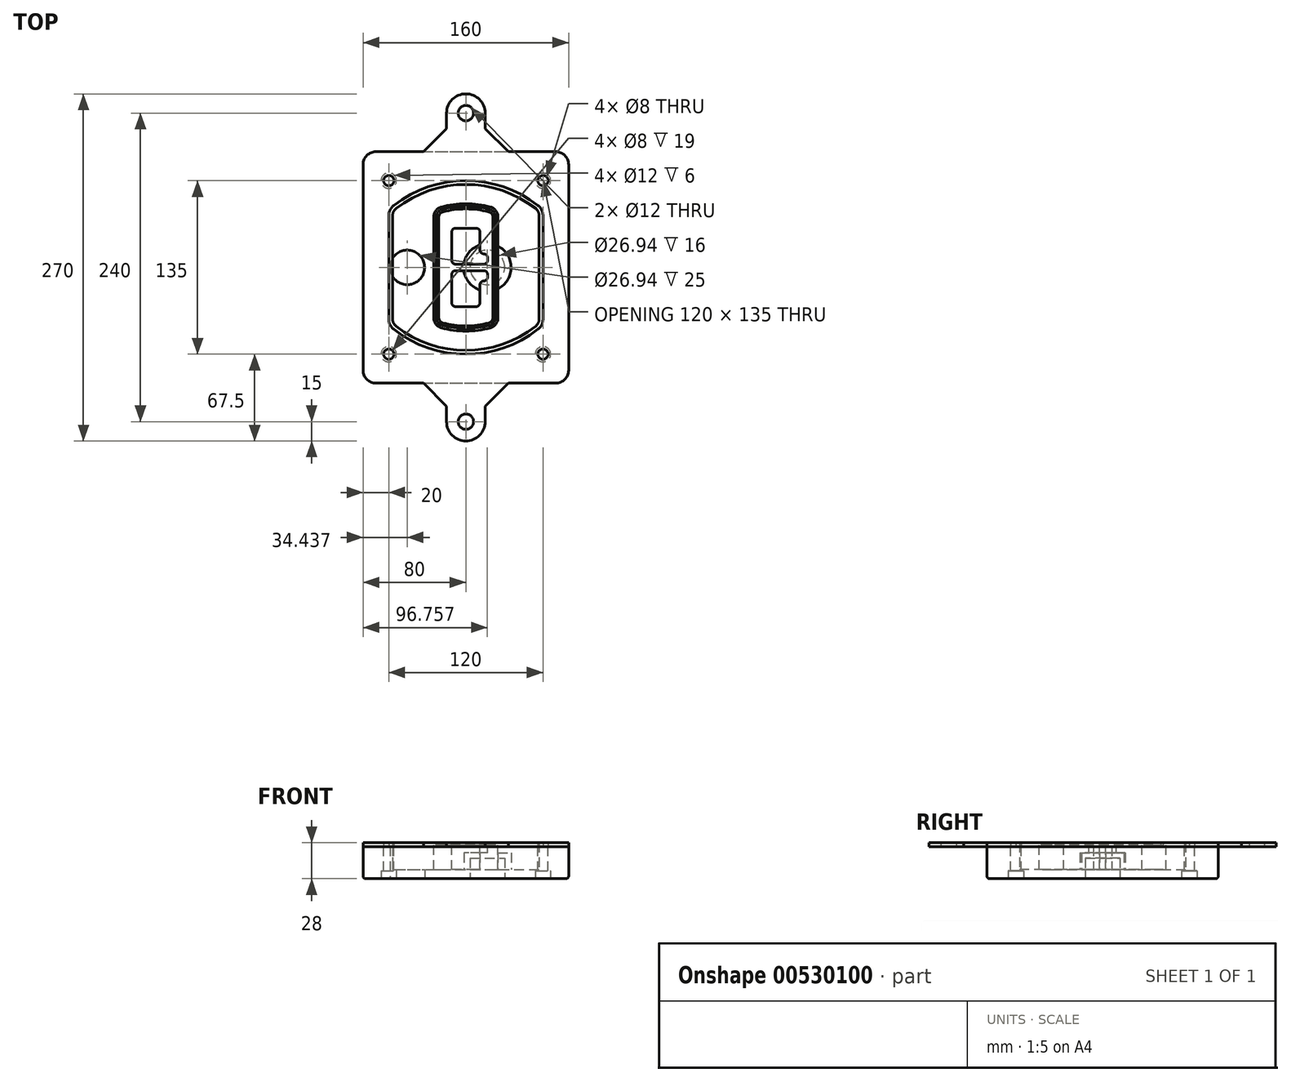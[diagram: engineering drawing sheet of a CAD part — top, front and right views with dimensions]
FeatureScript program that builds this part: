
annotation { "Feature Type Name" : "Feature", "Feature Type Description" : "" }
export const myFeature = defineFeature(function(context is Context, id is Id, definition is map)
    precondition{}
    {
        {
            var Q0;
            Q0=qCreatedBy(makeId("Top.planeOp"),FACE);
            var sketch = newSketch(context, id + "F0", { "sketchPlane" : qUnion([Q0])});
            skPoint(sketch, "E0.rect.middle", {"position": v(0, 0) * mm});
            skLineSegment(sketch, "E1.bottom", {"start": v(-70, -90) * mm, "end": v(70, -90) * mm});
            skLineSegment(sketch, "E1.top", {"start": v(-70, 90) * mm, "end": v(70, 90) * mm});
            skLineSegment(sketch, "E1.left", {"start": v(-80, -80) * mm, "end": v(-80, 80) * mm});
            skLineSegment(sketch, "E1.right", {"start": v(80, -80) * mm, "end": v(80, 80) * mm});
            skLineSegment(sketch, "E2", {"start": v(-80, 90) * mm, "end": v(80, -90) * mm, "construction": true});
            skLineSegment(sketch, "E3", {"start": v(80, 90) * mm, "end": v(-80, -90) * mm, "construction": true});
            skCircle(sketch, "E4", {"center": v(-60, 67.5) * mm, "radius": 4 * mm});
            skCircle(sketch, "E5", {"center": v(60, 67.5) * mm, "radius": 4 * mm});
            skCircle(sketch, "E6", {"center": v(60, -67.5) * mm, "radius": 4 * mm});
            skCircle(sketch, "E7", {"center": v(-60, -67.5) * mm, "radius": 4 * mm});
            skLineSegment(sketch, "E8", {"start": v(-60, 67.5) * mm, "end": v(60, 67.5) * mm, "construction": true});
            skLineSegment(sketch, "E9", {"start": v(60, 67.5) * mm, "end": v(60, -67.5) * mm, "construction": true});
            skLineSegment(sketch, "E10", {"start": v(60, -67.5) * mm, "end": v(-60, -67.5) * mm, "construction": true});
            skLineSegment(sketch, "E11", {"start": v(-60, -67.5) * mm, "end": v(-60, 67.5) * mm, "construction": true});
            skLineSegment(sketch, "E12", {"start": v(-60, 40.3) * mm, "end": v(-60, -40.3) * mm});
            skLineSegment(sketch, "E13", {"start": v(60, 40.3) * mm, "end": v(60, -40.3) * mm});
            skArc(sketch, "E14", {"start": v(56.15, 48.18) * mm, "mid": v(0, 67.5) * mm, "end": v(-56.15, 48.18) * mm});
            skArc(sketch, "E15", {"start": v(-56.15, -48.18) * mm, "mid": v(0, -67.5) * mm, "end": v(56.15, -48.18) * mm});
            skLineSegment(sketch, "E16", {"start": v(-60, 0) * mm, "end": v(60, 0) * mm, "construction": true});
            skPoint(sketch, "E17.visualSharp", {"position": v(-60, -45) * mm});
            skArc(sketch, "E17.filletArc", {"start": v(-60, -40.3) * mm, "mid": v(-58.99, -44.68) * mm, "end": v(-56.15, -48.18) * mm});
            skPoint(sketch, "E18.visualSharp", {"position": v(-60, 45) * mm});
            skArc(sketch, "E18.filletArc", {"start": v(-56.15, 48.18) * mm, "mid": v(-58.99, 44.68) * mm, "end": v(-60, 40.3) * mm});
            skPoint(sketch, "E19.visualSharp", {"position": v(60, 45) * mm});
            skArc(sketch, "E19.filletArc", {"start": v(60, 40.3) * mm, "mid": v(58.99, 44.68) * mm, "end": v(56.15, 48.18) * mm});
            skPoint(sketch, "E20.visualSharp", {"position": v(60, -45) * mm});
            skArc(sketch, "E20.filletArc", {"start": v(56.15, -48.18) * mm, "mid": v(58.99, -44.68) * mm, "end": v(60, -40.3) * mm});
            skPoint(sketch, "E21.visualSharp", {"position": v(-80, 90) * mm});
            skArc(sketch, "E21.filletArc", {"start": v(-70, 90) * mm, "mid": v(-77.07, 87.07) * mm, "end": v(-80, 80) * mm});
            skPoint(sketch, "E22.visualSharp", {"position": v(80, 90) * mm});
            skArc(sketch, "E22.filletArc", {"start": v(80, 80) * mm, "mid": v(77.07, 87.07) * mm, "end": v(70, 90) * mm});
            skPoint(sketch, "E23.visualSharp", {"position": v(80, -90) * mm});
            skArc(sketch, "E23.filletArc", {"start": v(70, -90) * mm, "mid": v(77.07, -87.07) * mm, "end": v(80, -80) * mm});
            skPoint(sketch, "E24.visualSharp", {"position": v(-80, -90) * mm});
            skArc(sketch, "E24.filletArc", {"start": v(-80, -80) * mm, "mid": v(-77.07, -87.07) * mm, "end": v(-70, -90) * mm});
            skArc(sketch, "E25.0", {"start": v(57, 40.3) * mm, "mid": v(56.3, 43.36) * mm, "end": v(54.3, 45.81) * mm});
            skLineSegment(sketch, "E25.1", {"start": v(57, 40.3) * mm, "end": v(57, -40.3) * mm});
            skArc(sketch, "E25.2", {"start": v(54.3, -45.81) * mm, "mid": v(56.3, -43.36) * mm, "end": v(57, -40.3) * mm});
            skArc(sketch, "E25.3", {"start": v(-54.3, -45.81) * mm, "mid": v(0, -64.5) * mm, "end": v(54.3, -45.81) * mm});
            skArc(sketch, "E25.4", {"start": v(-57, -40.3) * mm, "mid": v(-56.3, -43.36) * mm, "end": v(-54.3, -45.81) * mm});
            skArc(sketch, "E25.5", {"start": v(54.3, 45.81) * mm, "mid": v(0, 64.5) * mm, "end": v(-54.3, 45.81) * mm});
            skLineSegment(sketch, "E25.6", {"start": v(-57, 40.3) * mm, "end": v(-57, -40.3) * mm});
            skArc(sketch, "E25.7", {"start": v(-54.3, 45.81) * mm, "mid": v(-56.3, 43.36) * mm, "end": v(-57, 40.3) * mm});
            skArc(sketch, "E26.0", {"start": v(-58.62, 51.33) * mm, "mid": v(-62.58, 46.43) * mm, "end": v(-64, 40.3) * mm});
            skArc(sketch, "E26.1", {"start": v(58.62, 51.33) * mm, "mid": v(0, 71.5) * mm, "end": v(-58.62, 51.33) * mm});
            skArc(sketch, "E26.2", {"start": v(64, 40.3) * mm, "mid": v(62.58, 46.43) * mm, "end": v(58.62, 51.33) * mm});
            skLineSegment(sketch, "E26.3", {"start": v(64, 40.3) * mm, "end": v(64, -40.3) * mm});
            skArc(sketch, "E26.4", {"start": v(58.62, -51.33) * mm, "mid": v(62.58, -46.43) * mm, "end": v(64, -40.3) * mm});
            skLineSegment(sketch, "E26.5", {"start": v(-64, 40.3) * mm, "end": v(-64, -40.3) * mm});
            skArc(sketch, "E26.6", {"start": v(-58.62, -51.33) * mm, "mid": v(0, -71.5) * mm, "end": v(58.62, -51.33) * mm});
            skArc(sketch, "E26.7", {"start": v(-64, -40.3) * mm, "mid": v(-62.58, -46.43) * mm, "end": v(-58.62, -51.33) * mm});
            skSolve(sketch);
        }
        {
            var Q0;
            Q0=makeQuery(id+"F0.imprint","IMPRINT",FACE,{"disambiguationData":[TD([[makeQuery(id+"F0.imprint","IMPRINT",EDGE,{"derivedFrom":sQuery(id+"F0.wireOp",EDGE,"E1.bottom")}),1.0]])]});
            var Q1;
            Q1=makeQuery(id+"F0.imprint","IMPRINT",FACE,{"disambiguationData":[TD([[makeQuery(id+"F0.imprint","IMPRINT",EDGE,{"derivedFrom":sQuery(id+"F0.wireOp",EDGE,"E12")}),1.0]])]});
            var Q2;
            Q2=makeQuery(id+"F0.imprint","IMPRINT",FACE,{"disambiguationData":[TD([[makeQuery(id+"F0.imprint","IMPRINT",EDGE,{"derivedFrom":sQuery(id+"F0.wireOp",EDGE,"E25.0")}),1.0]])]});
            var Q3;
            Q3=makeQuery(id+"F0.imprint","IMPRINT",FACE,{"disambiguationData":[TD([[makeQuery(id+"F0.imprint","IMPRINT",EDGE,{"derivedFrom":sQuery(id+"F0.wireOp",EDGE,"E12")}),-1.0]])]});
            extrude(context, id + "F1", {"entities" : qUnion([Q0, Q1, Q2, Q3]), "oppositeDirection" : true, "depth" : 25 * mm});
        }
        {
            var Q0;
            Q0=makeQuery(id+"F0.imprint","IMPRINT",FACE,{"disambiguationData":[TD([[makeQuery(id+"F0.imprint","IMPRINT",EDGE,{"derivedFrom":sQuery(id+"F0.wireOp",EDGE,"E12")}),1.0]])]});
            extrude(context, id + "F2", {"entities" : qUnion([Q0]), "operationType" : NewBodyOperationType.ADD, "depth" : 3 * mm, "offsetDistance" : 25 * mm});
        }
        {
            var Q0;
            Q0=makeQuery(id+"F0.imprint","IMPRINT",FACE,{"disambiguationData":[TD([[makeQuery(id+"F0.imprint","IMPRINT",EDGE,{"derivedFrom":sQuery(id+"F0.wireOp",EDGE,"E25.0")}),1.0]])]});
            extrude(context, id + "F3", {"entities" : qUnion([Q0]), "operationType" : NewBodyOperationType.REMOVE, "oppositeDirection" : true, "depth" : 18 * mm});
        }
        {
            var Q0;
            Q0=makeQuery(id+"F2.opExtrude","CAP_FACE",FACE,{"disambiguationData":[OSD([sQuery(id+"F0.wireOp",EDGE,"E12"),sQuery(id+"F0.wireOp",EDGE,"E13"),sQuery(id+"F0.wireOp",EDGE,"E14"),sQuery(id+"F0.wireOp",EDGE,"E15"),sQuery(id+"F0.wireOp",EDGE,"E17.filletArc"),sQuery(id+"F0.wireOp",EDGE,"E18.filletArc"),sQuery(id+"F0.wireOp",EDGE,"E19.filletArc"),sQuery(id+"F0.wireOp",EDGE,"E20.filletArc"),sQuery(id+"F0.wireOp",EDGE,"E25.0"),sQuery(id+"F0.wireOp",EDGE,"E25.1"),sQuery(id+"F0.wireOp",EDGE,"E25.2"),sQuery(id+"F0.wireOp",EDGE,"E25.3"),sQuery(id+"F0.wireOp",EDGE,"E25.4"),sQuery(id+"F0.wireOp",EDGE,"E25.5"),sQuery(id+"F0.wireOp",EDGE,"E25.6"),sQuery(id+"F0.wireOp",EDGE,"E25.7")])],"isStart":false});
            var sketch = newSketch(context, id + "F4", { "sketchPlane" : qUnion([Q0])});
            skArc(sketch, "E27.0", {"start": v(-19.08, -46.97) * mm, "mid": v(0, -49.5) * mm, "end": v(19.08, -46.97) * mm});
            skArc(sketch, "E28.0", {"start": v(19.08, 46.97) * mm, "mid": v(0, 49.5) * mm, "end": v(-19.08, 46.97) * mm});
            skLineSegment(sketch, "E29", {"start": v(-25, 39.25) * mm, "end": v(-25, -39.25) * mm});
            skLineSegment(sketch, "E30", {"start": v(25, 39.25) * mm, "end": v(25, -39.25) * mm});
            skLineSegment(sketch, "E31", {"start": v(-25, 45.1) * mm, "end": v(25, 45.1) * mm, "construction": true});
            skLineSegment(sketch, "E32", {"start": v(-25, -45.1) * mm, "end": v(25, -45.1) * mm, "construction": true});
            skPoint(sketch, "E33.visualSharp", {"position": v(-25, 45.1) * mm});
            skArc(sketch, "E33.filletArc", {"start": v(-19.08, 46.97) * mm, "mid": v(-23.35, 44.11) * mm, "end": v(-25, 39.25) * mm});
            skPoint(sketch, "E34.visualSharp", {"position": v(25, 45.1) * mm});
            skArc(sketch, "E34.filletArc", {"start": v(25, 39.25) * mm, "mid": v(23.35, 44.11) * mm, "end": v(19.08, 46.97) * mm});
            skPoint(sketch, "E35.visualSharp", {"position": v(25, -45.1) * mm});
            skArc(sketch, "E35.filletArc", {"start": v(19.08, -46.97) * mm, "mid": v(23.35, -44.11) * mm, "end": v(25, -39.25) * mm});
            skPoint(sketch, "E36.visualSharp", {"position": v(-25, -45.1) * mm});
            skArc(sketch, "E36.filletArc", {"start": v(-25, -39.25) * mm, "mid": v(-23.35, -44.11) * mm, "end": v(-19.08, -46.97) * mm});
            skArc(sketch, "E37.0", {"start": v(54.3, 45.81) * mm, "mid": v(0, 64.5) * mm, "end": v(-54.3, 45.81) * mm});
            skArc(sketch, "E37.1", {"start": v(-54.3, 45.81) * mm, "mid": v(-56.3, 43.36) * mm, "end": v(-57, 40.3) * mm});
            skLineSegment(sketch, "E37.2", {"start": v(-57, 40.3) * mm, "end": v(-57, -40.3) * mm});
            skArc(sketch, "E37.3", {"start": v(-57, -40.3) * mm, "mid": v(-56.3, -43.36) * mm, "end": v(-54.3, -45.81) * mm});
            skArc(sketch, "E37.4", {"start": v(-54.3, -45.81) * mm, "mid": v(0, -64.5) * mm, "end": v(54.3, -45.81) * mm});
            skArc(sketch, "E37.5", {"start": v(54.3, -45.81) * mm, "mid": v(56.3, -43.36) * mm, "end": v(57, -40.3) * mm});
            skLineSegment(sketch, "E37.6", {"start": v(57, 40.3) * mm, "end": v(57, -40.3) * mm});
            skArc(sketch, "E37.7", {"start": v(57, 40.3) * mm, "mid": v(56.3, 43.36) * mm, "end": v(54.3, 45.81) * mm});
            skLineSegment(sketch, "E38.0", {"start": v(23, 39.25) * mm, "end": v(23, -39.25) * mm});
            skArc(sketch, "E38.1", {"start": v(18.56, -45.04) * mm, "mid": v(21.76, -42.9) * mm, "end": v(23, -39.25) * mm});
            skArc(sketch, "E38.2", {"start": v(-18.56, -45.04) * mm, "mid": v(0, -47.5) * mm, "end": v(18.56, -45.04) * mm});
            skArc(sketch, "E38.3", {"start": v(-23, -39.25) * mm, "mid": v(-21.76, -42.9) * mm, "end": v(-18.56, -45.04) * mm});
            skLineSegment(sketch, "E38.4", {"start": v(-23, 39.25) * mm, "end": v(-23, -39.25) * mm});
            skArc(sketch, "E38.5", {"start": v(23, 39.25) * mm, "mid": v(21.76, 42.9) * mm, "end": v(18.56, 45.04) * mm});
            skArc(sketch, "E38.6", {"start": v(-18.56, 45.04) * mm, "mid": v(-21.76, 42.9) * mm, "end": v(-23, 39.25) * mm});
            skArc(sketch, "E38.7", {"start": v(18.56, 45.04) * mm, "mid": v(0, 47.5) * mm, "end": v(-18.56, 45.04) * mm});
            skArc(sketch, "E39.0", {"start": v(21, 39.25) * mm, "mid": v(20.18, 41.68) * mm, "end": v(18.04, 43.1) * mm});
            skLineSegment(sketch, "E39.1", {"start": v(21, 39.25) * mm, "end": v(21, -39.25) * mm});
            skArc(sketch, "E39.2", {"start": v(18.04, -43.1) * mm, "mid": v(20.18, -41.68) * mm, "end": v(21, -39.25) * mm});
            skArc(sketch, "E39.3", {"start": v(-18.04, -43.1) * mm, "mid": v(0, -45.5) * mm, "end": v(18.04, -43.1) * mm});
            skArc(sketch, "E39.4", {"start": v(-21, -39.25) * mm, "mid": v(-20.18, -41.68) * mm, "end": v(-18.04, -43.1) * mm});
            skArc(sketch, "E39.5", {"start": v(18.04, 43.1) * mm, "mid": v(0, 45.5) * mm, "end": v(-18.04, 43.1) * mm});
            skLineSegment(sketch, "E39.6", {"start": v(-21, 39.25) * mm, "end": v(-21, -39.25) * mm});
            skArc(sketch, "E39.7", {"start": v(-18.04, 43.1) * mm, "mid": v(-20.18, 41.68) * mm, "end": v(-21, 39.25) * mm});
            skLineSegment(sketch, "E40", {"start": v(-25, 0) * mm, "end": v(25, 0) * mm, "construction": true});
            skLineSegment(sketch, "E41", {"start": v(-11, 5.5) * mm, "end": v(-11, 27.5) * mm});
            skLineSegment(sketch, "E42", {"start": v(-8, 30.5) * mm, "end": v(8, 30.5) * mm});
            skLineSegment(sketch, "E43", {"start": v(11, 27.5) * mm, "end": v(11, 13.5) * mm});
            skLineSegment(sketch, "E44", {"start": v(14, 10.5) * mm, "end": v(14, 10.5) * mm});
            skLineSegment(sketch, "E45", {"start": v(17, 7.5) * mm, "end": v(17, 5.5) * mm});
            skLineSegment(sketch, "E46", {"start": v(14, 2.5) * mm, "end": v(-8, 2.5) * mm});
            skPoint(sketch, "E47.visualSharp", {"position": v(-11, 30.5) * mm});
            skArc(sketch, "E47.filletArc", {"start": v(-8, 30.5) * mm, "mid": v(-10.12, 29.62) * mm, "end": v(-11, 27.5) * mm});
            skPoint(sketch, "E48.visualSharp", {"position": v(11, 30.5) * mm});
            skArc(sketch, "E48.filletArc", {"start": v(11, 27.5) * mm, "mid": v(10.12, 29.62) * mm, "end": v(8, 30.5) * mm});
            skPoint(sketch, "E49.visualSharp", {"position": v(11, 10.5) * mm});
            skArc(sketch, "E49.filletArc", {"start": v(11, 13.5) * mm, "mid": v(11.88, 11.38) * mm, "end": v(14, 10.5) * mm});
            skPoint(sketch, "E50.visualSharp", {"position": v(17, 10.5) * mm});
            skArc(sketch, "E50.filletArc", {"start": v(17, 7.5) * mm, "mid": v(16.12, 9.62) * mm, "end": v(14, 10.5) * mm});
            skPoint(sketch, "E51.visualSharp", {"position": v(17, 2.5) * mm});
            skArc(sketch, "E51.filletArc", {"start": v(14, 2.5) * mm, "mid": v(16.12, 3.38) * mm, "end": v(17, 5.5) * mm});
            skPoint(sketch, "E52.visualSharp", {"position": v(-11, 2.5) * mm});
            skArc(sketch, "E52.filletArc", {"start": v(-11, 5.5) * mm, "mid": v(-10.12, 3.38) * mm, "end": v(-8, 2.5) * mm});
            skLineSegment(sketch, "E53.0.MirrorCS", {"start": v(14, -2.5) * mm, "end": v(-8, -2.5) * mm});
            skArc(sketch, "E54.0.MirrorCS", {"start": v(-11, -5.5) * mm, "mid": v(-10.12, -3.38) * mm, "end": v(-8, -2.5) * mm});
            skLineSegment(sketch, "E55.0.MirrorCS", {"start": v(-11, -5.5) * mm, "end": v(-11, -27.5) * mm});
            skArc(sketch, "E56.0.MirrorCS", {"start": v(-8, -30.5) * mm, "mid": v(-10.12, -29.62) * mm, "end": v(-11, -27.5) * mm});
            skLineSegment(sketch, "E57.0.MirrorCS", {"start": v(-8, -30.5) * mm, "end": v(8, -30.5) * mm});
            skArc(sketch, "E58.0.MirrorCS", {"start": v(11, -27.5) * mm, "mid": v(10.12, -29.62) * mm, "end": v(8, -30.5) * mm});
            skLineSegment(sketch, "E59.0.MirrorCS", {"start": v(11, -27.5) * mm, "end": v(11, -13.5) * mm});
            skArc(sketch, "E60.0.MirrorCS", {"start": v(11, -13.5) * mm, "mid": v(11.88, -11.38) * mm, "end": v(14, -10.5) * mm});
            skArc(sketch, "E61.0.MirrorCS", {"start": v(17, -7.5) * mm, "mid": v(16.12, -9.62) * mm, "end": v(14, -10.5) * mm});
            skLineSegment(sketch, "E62.0.MirrorCS", {"start": v(17, -7.5) * mm, "end": v(17, -5.5) * mm});
            skArc(sketch, "E63.0.MirrorCS", {"start": v(14, -2.5) * mm, "mid": v(16.12, -3.38) * mm, "end": v(17, -5.5) * mm});
            skSolve(sketch);
        }
        {
            var Q0;
            Q0=makeQuery(id+"F4.imprint","IMPRINT",FACE,{"disambiguationData":[TD([[makeQuery(id+"F4.imprint","IMPRINT",EDGE,{"derivedFrom":sQuery(id+"F4.wireOp",EDGE,"E27.0")}),1.0]])]});
            var Q1;
            Q1=makeQuery(id+"F4.imprint","IMPRINT",FACE,{"disambiguationData":[TD([[makeQuery(id+"F4.imprint","IMPRINT",EDGE,{"derivedFrom":sQuery(id+"F4.wireOp",EDGE,"E38.0")}),-1.0]])]});
            var Q2;
            Q2=makeQuery(id+"F4.imprint","IMPRINT",FACE,{"disambiguationData":[TD([[makeQuery(id+"F4.imprint","IMPRINT",EDGE,{"derivedFrom":sQuery(id+"F4.wireOp",EDGE,"E39.0")}),1.0]])]});
            extrude(context, id + "F5", {"entities" : qUnion([Q0, Q1, Q2]), "operationType" : NewBodyOperationType.ADD, "endBound" : BoundingType.UP_TO_NEXT, "oppositeDirection" : true, "depth" : 25 * mm});
        }
        {
            var Q0;
            Q0=makeQuery(id+"F4.imprint","IMPRINT",FACE,{"disambiguationData":[TD([[makeQuery(id+"F4.imprint","IMPRINT",EDGE,{"derivedFrom":sQuery(id+"F4.wireOp",EDGE,"E38.0")}),-1.0]])]});
            extrude(context, id + "F6", {"entities" : qUnion([Q0]), "operationType" : NewBodyOperationType.REMOVE, "oppositeDirection" : true, "depth" : 2 * mm});
        }
        {
            var Q0;
            Q0=makeQuery(id+"F1.opExtrude","CAP_FACE",FACE,{"disambiguationData":[OSD([sQuery(id+"F0.wireOp",EDGE,"E1.bottom"),sQuery(id+"F0.wireOp",EDGE,"E1.top"),sQuery(id+"F0.wireOp",EDGE,"E1.left"),sQuery(id+"F0.wireOp",EDGE,"E1.right"),sQuery(id+"F0.wireOp",EDGE,"E4"),sQuery(id+"F0.wireOp",EDGE,"E5"),sQuery(id+"F0.wireOp",EDGE,"E6"),sQuery(id+"F0.wireOp",EDGE,"E7"),sQuery(id+"F0.wireOp",EDGE,"E21.filletArc"),sQuery(id+"F0.wireOp",EDGE,"E22.filletArc"),sQuery(id+"F0.wireOp",EDGE,"E23.filletArc"),sQuery(id+"F0.wireOp",EDGE,"E24.filletArc")])],"isStart":false});
            var sketch = newSketch(context, id + "F7", { "sketchPlane" : qUnion([Q0])});
            skCircle(sketch, "E64", {"center": v(16.76, 0) * mm, "radius": 13.47 * mm});
            skCircle(sketch, "E65", {"center": v(-45.56, 0) * mm, "radius": 13.47 * mm});
            skLineSegment(sketch, "E66", {"start": v(80, 0) * mm, "end": v(-80, 0) * mm});
            skCircle(sketch, "E67", {"center": v(16.76, 0) * mm, "radius": 18.47 * mm});
            skCircle(sketch, "E68", {"center": v(60, -67.5) * mm, "radius": 6 * mm});
            skCircle(sketch, "E69", {"center": v(-60, -67.5) * mm, "radius": 6 * mm});
            skCircle(sketch, "E70", {"center": v(-60, 67.5) * mm, "radius": 6 * mm});
            skCircle(sketch, "E71", {"center": v(60, 67.5) * mm, "radius": 6 * mm});
            skSolve(sketch);
        }
        {
            var Q0;
            {var subQ1=sQuery(id+"F7.wireOp",EDGE,"E66");var subQ4=sQuery(id+"F7.wireOp",EDGE,"E64");var subQ6=makeQuery(id+"F7.imprint","INTERSECT",VERTEX,{"disambiguationData":[OD(0.0)],"derivedFrom":[subQ4,subQ1]});Q0=makeQuery(id+"F7.imprint","IMPRINT",FACE,{"disambiguationData":[TD([[makeQuery(id+"F7.imprint","IMPRINT",EDGE,{"disambiguationData":[TD([[subQ6,-1.0]])],"derivedFrom":subQ4}),-1.0]])]});}
            var Q1;
            {var subQ0=sQuery(id+"F7.wireOp",EDGE,"E66");var subQ1=sQuery(id+"F7.wireOp",EDGE,"E64");var subQ3=makeQuery(id+"F7.imprint","INTERSECT",VERTEX,{"disambiguationData":[OD(0.0)],"derivedFrom":[subQ1,subQ0]});Q1=makeQuery(id+"F7.imprint","IMPRINT",FACE,{"disambiguationData":[TD([[makeQuery(id+"F7.imprint","IMPRINT",EDGE,{"disambiguationData":[TD([[subQ3,-1.0]])],"derivedFrom":subQ1}),1.0]])]});}
            var Q2;
            {var subQ0=sQuery(id+"F7.wireOp",EDGE,"E66");var subQ1=sQuery(id+"F7.wireOp",EDGE,"E64");var subQ3=makeQuery(id+"F7.imprint","INTERSECT",VERTEX,{"disambiguationData":[OD(0.0)],"derivedFrom":[subQ1,subQ0]});Q2=makeQuery(id+"F7.imprint","IMPRINT",FACE,{"disambiguationData":[TD([[makeQuery(id+"F7.imprint","IMPRINT",EDGE,{"disambiguationData":[TD([[subQ3,1.0]])],"derivedFrom":subQ1}),1.0]])]});}
            var Q3;
            {var subQ1=sQuery(id+"F7.wireOp",EDGE,"E66");var subQ4=sQuery(id+"F7.wireOp",EDGE,"E64");var subQ6=makeQuery(id+"F7.imprint","INTERSECT",VERTEX,{"disambiguationData":[OD(0.0)],"derivedFrom":[subQ4,subQ1]});Q3=makeQuery(id+"F7.imprint","IMPRINT",FACE,{"disambiguationData":[TD([[makeQuery(id+"F7.imprint","IMPRINT",EDGE,{"disambiguationData":[TD([[subQ6,1.0]])],"derivedFrom":subQ4}),-1.0]])]});}
            extrude(context, id + "F8", {"entities" : qUnion([Q0, Q1, Q2, Q3]), "operationType" : NewBodyOperationType.ADD, "oppositeDirection" : true, "depth" : 20 * mm});
        }
        {
            var Q0;
            {var subQ0=sQuery(id+"F7.wireOp",EDGE,"E66");var subQ1=sQuery(id+"F7.wireOp",EDGE,"E64");var subQ3=makeQuery(id+"F7.imprint","INTERSECT",VERTEX,{"disambiguationData":[OD(0.0)],"derivedFrom":[subQ1,subQ0]});Q0=makeQuery(id+"F7.imprint","IMPRINT",FACE,{"disambiguationData":[TD([[makeQuery(id+"F7.imprint","IMPRINT",EDGE,{"disambiguationData":[TD([[subQ3,-1.0]])],"derivedFrom":subQ1}),1.0]])]});}
            var Q1;
            {var subQ0=sQuery(id+"F7.wireOp",EDGE,"E66");var subQ1=sQuery(id+"F7.wireOp",EDGE,"E64");var subQ3=makeQuery(id+"F7.imprint","INTERSECT",VERTEX,{"disambiguationData":[OD(0.0)],"derivedFrom":[subQ1,subQ0]});Q1=makeQuery(id+"F7.imprint","IMPRINT",FACE,{"disambiguationData":[TD([[makeQuery(id+"F7.imprint","IMPRINT",EDGE,{"disambiguationData":[TD([[subQ3,1.0]])],"derivedFrom":subQ1}),1.0]])]});}
            extrude(context, id + "F9", {"entities" : qUnion([Q0, Q1]), "operationType" : NewBodyOperationType.REMOVE, "oppositeDirection" : true, "depth" : 16 * mm});
        }
        {
            var Q0;
            {var subQ0=sQuery(id+"F7.wireOp",EDGE,"E66");var subQ1=sQuery(id+"F7.wireOp",EDGE,"E65");var subQ3=makeQuery(id+"F7.imprint","INTERSECT",VERTEX,{"disambiguationData":[OD(0.0)],"derivedFrom":[subQ1,subQ0]});Q0=makeQuery(id+"F7.imprint","IMPRINT",FACE,{"disambiguationData":[TD([[makeQuery(id+"F7.imprint","IMPRINT",EDGE,{"disambiguationData":[TD([[subQ3,-1.0]])],"derivedFrom":subQ1}),1.0]])]});}
            var Q1;
            {var subQ0=sQuery(id+"F7.wireOp",EDGE,"E66");var subQ1=sQuery(id+"F7.wireOp",EDGE,"E65");var subQ3=makeQuery(id+"F7.imprint","INTERSECT",VERTEX,{"disambiguationData":[OD(0.0)],"derivedFrom":[subQ1,subQ0]});Q1=makeQuery(id+"F7.imprint","IMPRINT",FACE,{"disambiguationData":[TD([[makeQuery(id+"F7.imprint","IMPRINT",EDGE,{"disambiguationData":[TD([[subQ3,1.0]])],"derivedFrom":subQ1}),1.0]])]});}
            extrude(context, id + "F10", {"entities" : qUnion([Q0, Q1]), "operationType" : NewBodyOperationType.REMOVE, "oppositeDirection" : true, "depth" : 25 * mm});
        }
        {
            var Q0;
            Q0=makeQuery(id+"F7.imprint","IMPRINT",FACE,{"disambiguationData":[TD([[makeQuery(id+"F7.imprint","IMPRINT",EDGE,{"derivedFrom":sQuery(id+"F7.wireOp",EDGE,"E68")}),1.0]])]});
            var Q1;
            Q1=makeQuery(id+"F7.imprint","IMPRINT",FACE,{"disambiguationData":[TD([[makeQuery(id+"F7.imprint","IMPRINT",EDGE,{"derivedFrom":makeQuery(id+"F1.opExtrude","CAP_EDGE",EDGE,{"disambiguationData":[OSD([sQuery(id+"F0.wireOp",EDGE,"E5")])],"isStart":false})}),-1.0]])]});
            var Q2;
            Q2=makeQuery(id+"F7.imprint","IMPRINT",FACE,{"disambiguationData":[TD([[makeQuery(id+"F7.imprint","IMPRINT",EDGE,{"derivedFrom":sQuery(id+"F7.wireOp",EDGE,"E69")}),1.0]])]});
            var Q3;
            Q3=makeQuery(id+"F7.imprint","IMPRINT",FACE,{"disambiguationData":[TD([[makeQuery(id+"F7.imprint","IMPRINT",EDGE,{"derivedFrom":makeQuery(id+"F1.opExtrude","CAP_EDGE",EDGE,{"disambiguationData":[OSD([sQuery(id+"F0.wireOp",EDGE,"E4")])],"isStart":false})}),-1.0]])]});
            var Q4;
            Q4=makeQuery(id+"F7.imprint","IMPRINT",FACE,{"disambiguationData":[TD([[makeQuery(id+"F7.imprint","IMPRINT",EDGE,{"derivedFrom":sQuery(id+"F7.wireOp",EDGE,"E70")}),1.0]])]});
            var Q5;
            Q5=makeQuery(id+"F7.imprint","IMPRINT",FACE,{"disambiguationData":[TD([[makeQuery(id+"F7.imprint","IMPRINT",EDGE,{"derivedFrom":makeQuery(id+"F1.opExtrude","CAP_EDGE",EDGE,{"disambiguationData":[OSD([sQuery(id+"F0.wireOp",EDGE,"E7")])],"isStart":false})}),-1.0]])]});
            var Q6;
            Q6=makeQuery(id+"F7.imprint","IMPRINT",FACE,{"disambiguationData":[TD([[makeQuery(id+"F7.imprint","IMPRINT",EDGE,{"derivedFrom":sQuery(id+"F7.wireOp",EDGE,"E71")}),1.0]])]});
            var Q7;
            Q7=makeQuery(id+"F7.imprint","IMPRINT",FACE,{"disambiguationData":[TD([[makeQuery(id+"F7.imprint","IMPRINT",EDGE,{"derivedFrom":makeQuery(id+"F1.opExtrude","CAP_EDGE",EDGE,{"disambiguationData":[OSD([sQuery(id+"F0.wireOp",EDGE,"E6")])],"isStart":false})}),-1.0]])]});
            extrude(context, id + "F11", {"entities" : qUnion([Q0, Q1, Q2, Q3, Q4, Q5, Q6, Q7]), "operationType" : NewBodyOperationType.REMOVE, "oppositeDirection" : true, "depth" : 6 * mm});
        }
        {
            var Q0;
            Q0=makeQuery(id+"F1.opExtrude","CAP_EDGE",EDGE,{"disambiguationData":[OSD([sQuery(id+"F0.wireOp",EDGE,"E1.bottom")])],"isStart":false});
            fillet(context, id + "F12", {"entities" : qUnion([Q0]), "radius" : 2 * mm, "tangentPropagation" : true, "allowEdgeOverflow" : false});
        }
        {
            var Q0;
            {var subQ0=sQuery(id+"F0.wireOp",EDGE,"E21.filletArc");var subQ1=sQuery(id+"F0.wireOp",EDGE,"E7");var subQ2=sQuery(id+"F0.wireOp",EDGE,"E6");var subQ3=sQuery(id+"F0.wireOp",EDGE,"E5");var subQ4=sQuery(id+"F0.wireOp",EDGE,"E4");var subQ5=sQuery(id+"F0.wireOp",EDGE,"E22.filletArc");var subQ6=sQuery(id+"F0.wireOp",EDGE,"E1.bottom");var subQ7=sQuery(id+"F0.wireOp",EDGE,"E1.right");var subQ8=sQuery(id+"F0.wireOp",EDGE,"E1.top");var subQ9=sQuery(id+"F0.wireOp",EDGE,"E1.left");var subQ10=sQuery(id+"F0.wireOp",EDGE,"E23.filletArc");var subQ11=sQuery(id+"F0.wireOp",EDGE,"E24.filletArc");Q0=makeQuery(id+"F2.boolean.opBoolean","SPLIT",FACE,{"disambiguationData":[TD([makeQuery(id+"F1.opExtrude","SWEPT_FACE",FACE,{"disambiguationData":[OSD([subQ6])]})])],"derivedFrom":makeQuery(id+"F1.opExtrude","CAP_FACE",FACE,{"disambiguationData":[OSD([subQ6,subQ8,subQ9,subQ7,subQ4,subQ3,subQ2,subQ1,subQ0,subQ5,subQ10,subQ11])],"isStart":true})});}
            var sketch = newSketch(context, id + "F13", { "sketchPlane" : qUnion([Q0])});
            skLineSegment(sketch, "E72", {"start": v(-33, 90) * mm, "end": v(-15, 108) * mm});
            skLineSegment(sketch, "E73", {"start": v(-15, 108) * mm, "end": v(-15, 120) * mm});
            skLineSegment(sketch, "E74", {"start": v(15, 120) * mm, "end": v(15, 108) * mm});
            skLineSegment(sketch, "E75", {"start": v(15, 108) * mm, "end": v(33, 90) * mm});
            skPoint(sketch, "E76.endSnap0", {"position": v(80, 0) * mm});
            skCircle(sketch, "E77", {"center": v(0, 120) * mm, "radius": 6 * mm});
            skArc(sketch, "E78", {"start": v(15, 120) * mm, "mid": v(0, 135) * mm, "end": v(-15, 120) * mm});
            skLineSegment(sketch, "E79", {"start": v(80, 0) * mm, "end": v(-80, 0) * mm, "construction": true});
            skLineSegment(sketch, "E80.MirrorCS", {"start": v(-33, -90) * mm, "end": v(-15, -108) * mm});
            skLineSegment(sketch, "E81.MirrorCS", {"start": v(-15, -108) * mm, "end": v(-15, -120) * mm});
            skArc(sketch, "E82.MirrorCS", {"start": v(15, -120) * mm, "mid": v(0, -135) * mm, "end": v(-15, -120) * mm});
            skLineSegment(sketch, "E83.MirrorCS", {"start": v(15, -120) * mm, "end": v(15, -108) * mm});
            skLineSegment(sketch, "E84.MirrorCS", {"start": v(15, -108) * mm, "end": v(33, -90) * mm});
            skCircle(sketch, "E85.MirrorC", {"center": v(0, -120) * mm, "radius": 6 * mm});
            skArc(sketch, "E86.0", {"start": v(-70, 90) * mm, "mid": v(-77.07, 87.07) * mm, "end": v(-80, 80) * mm});
            skLineSegment(sketch, "E87.0", {"start": v(-80, -80) * mm, "end": v(-80, 80) * mm});
            skPoint(sketch, "E88.0", {"position": v(-77.07, -87.07) * mm});
            skLineSegment(sketch, "E89.0", {"start": v(-70, 90) * mm, "end": v(70, 90) * mm});
            skLineSegment(sketch, "E90.0", {"start": v(80, -80) * mm, "end": v(80, 80) * mm});
            skArc(sketch, "E90.1", {"start": v(80, 80) * mm, "mid": v(77.07, 87.07) * mm, "end": v(70, 90) * mm});
            skLineSegment(sketch, "E91.0", {"start": v(-70, -90) * mm, "end": v(70, -90) * mm});
            skArc(sketch, "E92.0", {"start": v(70, -90) * mm, "mid": v(77.07, -87.07) * mm, "end": v(80, -80) * mm});
            skArc(sketch, "E93.0", {"start": v(-80, -80) * mm, "mid": v(-77.07, -87.07) * mm, "end": v(-70, -90) * mm});
            skSolve(sketch);
        }
        {
            var Q0;
            {var subQ0=sQuery(id+"F13.wireOp",EDGE,"E80.MirrorCS");Q0=makeQuery(id+"F13.imprint","IMPRINT",FACE,{"disambiguationData":[TD([[makeQuery(id+"F13.imprint","IMPRINT",EDGE,{"derivedFrom":subQ0}),1.0]])]});}
            var Q1;
            {var subQ1=sQuery(id+"F13.wireOp",EDGE,"E72");Q1=makeQuery(id+"F13.imprint","IMPRINT",FACE,{"disambiguationData":[TD([[makeQuery(id+"F13.imprint","IMPRINT",EDGE,{"derivedFrom":subQ1}),-1.0]])]});}
            var Q2;
            Q2=makeQuery(id+"F13.imprint","IMPRINT",FACE,{"disambiguationData":[TD([[makeQuery(id+"F13.imprint","IMPRINT",EDGE,{"derivedFrom":makeQuery(id+"F1.opExtrude","CAP_EDGE",EDGE,{"disambiguationData":[OSD([sQuery(id+"F0.wireOp",EDGE,"E1.left")])],"isStart":true})}),-1.0]])]});
            var Q3;
            {var subQ11=sQuery(id+"F13.wireOp",EDGE,"E86.0");Q3=makeQuery(id+"F13.imprint","IMPRINT",FACE,{"disambiguationData":[TD([[makeQuery(id+"F13.imprint","IMPRINT",EDGE,{"derivedFrom":subQ11}),1.0]])]});}
            var Q4;
            Q4=makeQuery(id+"F2.opExtrude","CAP_FACE",FACE,{"disambiguationData":[OSD([sQuery(id+"F0.wireOp",EDGE,"E12"),sQuery(id+"F0.wireOp",EDGE,"E13"),sQuery(id+"F0.wireOp",EDGE,"E14"),sQuery(id+"F0.wireOp",EDGE,"E15"),sQuery(id+"F0.wireOp",EDGE,"E17.filletArc"),sQuery(id+"F0.wireOp",EDGE,"E18.filletArc"),sQuery(id+"F0.wireOp",EDGE,"E19.filletArc"),sQuery(id+"F0.wireOp",EDGE,"E20.filletArc"),sQuery(id+"F0.wireOp",EDGE,"E25.0"),sQuery(id+"F0.wireOp",EDGE,"E25.1"),sQuery(id+"F0.wireOp",EDGE,"E25.2"),sQuery(id+"F0.wireOp",EDGE,"E25.3"),sQuery(id+"F0.wireOp",EDGE,"E25.4"),sQuery(id+"F0.wireOp",EDGE,"E25.5"),sQuery(id+"F0.wireOp",EDGE,"E25.6"),sQuery(id+"F0.wireOp",EDGE,"E25.7")])],"isStart":false});
            var Q5;
            Q5=makeQuery(id+"F1.opExtrude","SWEPT_BODY",BODY,{"disambiguationData":[OSD([sQuery(id+"F0.wireOp",EDGE,"E1.bottom"),sQuery(id+"F0.wireOp",EDGE,"E1.top"),sQuery(id+"F0.wireOp",EDGE,"E1.left"),sQuery(id+"F0.wireOp",EDGE,"E1.right"),sQuery(id+"F0.wireOp",EDGE,"E4"),sQuery(id+"F0.wireOp",EDGE,"E5"),sQuery(id+"F0.wireOp",EDGE,"E6"),sQuery(id+"F0.wireOp",EDGE,"E7"),sQuery(id+"F0.wireOp",EDGE,"E21.filletArc"),sQuery(id+"F0.wireOp",EDGE,"E22.filletArc"),sQuery(id+"F0.wireOp",EDGE,"E23.filletArc"),sQuery(id+"F0.wireOp",EDGE,"E24.filletArc")])]});
            extrude(context, id + "F14", {"entities" : qUnion([Q0, Q1, Q2, Q3]), "endBound" : BoundingType.UP_TO_SURFACE, "depth" : 25 * mm, "endBoundEntityFace" : qUnion([Q4]), "endBoundEntityBody" : qUnion([Q5]), "offsetDistance" : 25 * mm});
        }
    });
